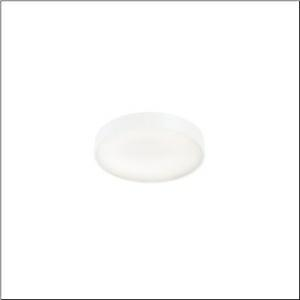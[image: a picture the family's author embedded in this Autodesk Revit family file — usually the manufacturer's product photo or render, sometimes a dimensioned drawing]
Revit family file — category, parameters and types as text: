
# Revit family: round_21_s_51mr34nd0321w
name_source: partatom
category: Lighting Fixtures
units: mm (PartAtom-declared; Revit-internal decimal feet)

## family parameters
Cut with Voids When Loaded = No
Host = Face
Light Source = No
Part Type = Normal
Room Calculation Point = No
Round Connector Dimension = Use Diameter
Shared = No

## types (1)
- Round 21 S (1 x LED, 3660 lm, 28.3 W, 3000K)
    Apparent Load = 28 VA
    CIE Flux Codes = 66 90 98 71 100
    Color Rendering = 80
    Color Temperature = 3000K
    Default Elevation = 1800 mm
    Description = Round 21 S, wall and ceiling luminaire, primary optical cover: micro prismatic cover, of PMMA, transparent, CAT 2 (L<= 3000cd/m²), light emission: direct/indirect distribution, primary light characteristic: symmetric, installation type: suspended mounting, surface-mounted, LED, rated luminous flux: 3.660lm, luminous efficacy: 129lm/W, light colour: 830, colour temperature: 3000K, control gear: DALI 2, with terminal, 5-pole, mains connection: 230V, AC, 50/60Hz, rated input power: 28.3W, housing, of aluminium, coated, white, diameter: 400mm, height: 62mm, protection rating (complete): IP40, insulation class (complete): insulation class I (protective earthing), certification: CE, impact resistance: IK04, permissible operating ambient temperature: -10..+35°C, packaging unit: 1 piece
    Height = 87 mm
    Lamp = 1 x LED
    Lamp Light Flux = 3660 lm
    Lamp Power = 28.3 W
    Lamp count = 1
    Length = 400 mm
    Luminous efficacy = 129 lm/W
    Manufacturer = Siteco
    ModVariant = No
    Model = 51MR34ND0321W
    Mounting Place = Ceiling
    Mounting Type = Surface mounted
    Number of Poles = 1
    OnlyDefault = Yes
    Power Factor = 1
    Product Name = Round 21 S
    Product group = wall and ceiling luminaire
    ProductGroupID = 304
    Protection Class = Protection class I
    Protection Degree = IP 40
    RLX_Detail_Level = 1
    RLX_Emergency_Light_Flux = 0 lm
    RLX_Emergency_Type = 0
    RLX_Emergency_Type_DB = No
    RlxData = <blob elided: 12841 chars, md5=eb054750>
    Socket = socket
    Standby Power = 0 W
    System Light Flux = 3660 lm
    System Power = 28 W
    Type Comments = Product without accessories
    Type Image = l_1258334.jpg
    URL = http://relux.com
    VarID = ---
    Voltage = 0 V
    Weight = 0.00 kg
    Width = 0 mm  [stored 0 ft]

note: [stored X ft] marks values corroborated as IEEE doubles in the binary element streams (Revit-internal decimal feet)

## geometry (parser evidence)
native form markers: Sweep x9
no freeform markers — native parametric forms only
